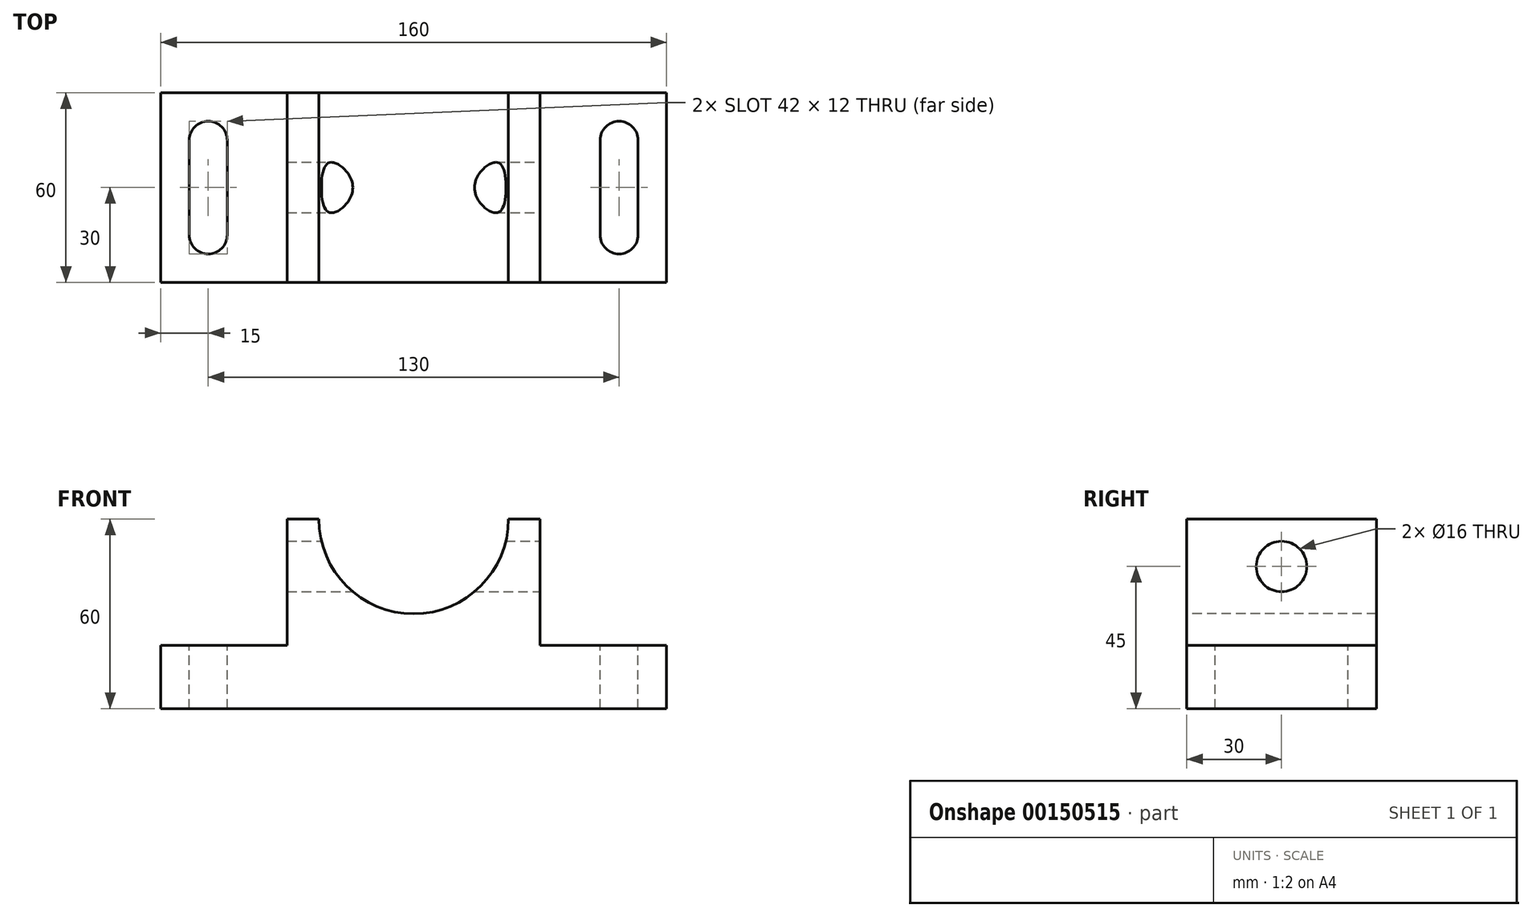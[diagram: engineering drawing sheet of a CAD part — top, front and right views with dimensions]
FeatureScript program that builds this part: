
annotation { "Feature Type Name" : "Feature", "Feature Type Description" : "" }
export const myFeature = defineFeature(function(context is Context, id is Id, definition is map)
    precondition{}
    {
        {
            var Q0;
            Q0=qCreatedBy(makeId("Top.planeOp"),FACE);
            var sketch = newSketch(context, id + "F0", { "sketchPlane" : qUnion([Q0])});
            skLineSegment(sketch, "E0.bottom", {"start": v(80, -30) * mm, "end": v(-80, -30) * mm});
            skLineSegment(sketch, "E0.top", {"start": v(80, 30) * mm, "end": v(-80, 30) * mm});
            skLineSegment(sketch, "E0.left", {"start": v(80, -30) * mm, "end": v(80, 30) * mm});
            skLineSegment(sketch, "E0.right", {"start": v(-80, -30) * mm, "end": v(-80, 30) * mm});
            skPoint(sketch, "E0.middle", {"position": v(0, 0) * mm});
            skSolve(sketch);
        }
        {
            var Q0;
            Q0 = qSketchRegion(id + "F0", true);
            extrude(context, id + "F1", {"entities" : qUnion([Q0]), "depth" : 20 * mm});
        }
        {
            var Q0;
            Q0=makeQuery(id+"F1.opExtrude","CAP_FACE",FACE,{"disambiguationData":[OSD([sQuery(id+"F0.wireOp",EDGE,"E0.bottom"),sQuery(id+"F0.wireOp",EDGE,"E0.top"),sQuery(id+"F0.wireOp",EDGE,"E0.left"),sQuery(id+"F0.wireOp",EDGE,"E0.right")])],"isStart":false});
            var sketch = newSketch(context, id + "F2", { "sketchPlane" : qUnion([Q0])});
            skLineSegment(sketch, "E1.left", {"start": v(-59, -15) * mm, "end": v(-59, 15) * mm});
            skLineSegment(sketch, "E1.right", {"start": v(-71, -15) * mm, "end": v(-71, 15) * mm});
            skPoint(sketch, "E1.middle", {"position": v(-65, 0) * mm});
            skLineSegment(sketch, "E2.left", {"start": v(71, -15) * mm, "end": v(71, 15) * mm});
            skLineSegment(sketch, "E2.right", {"start": v(59, -15) * mm, "end": v(59, 15) * mm});
            skPoint(sketch, "E2.middle", {"position": v(65, 0) * mm});
            skArc(sketch, "E3", {"start": v(-59, 15) * mm, "mid": v(-65, 21) * mm, "end": v(-71, 15) * mm});
            skArc(sketch, "E4", {"start": v(-71, -15) * mm, "mid": v(-65, -21) * mm, "end": v(-59, -15) * mm});
            skArc(sketch, "E5", {"start": v(71, 15) * mm, "mid": v(65, 21) * mm, "end": v(59, 15) * mm});
            skArc(sketch, "E6", {"start": v(59, -15) * mm, "mid": v(65, -21) * mm, "end": v(71, -15) * mm});
            skLineSegment(sketch, "E7.bottom", {"start": v(40, -30) * mm, "end": v(-40, -30) * mm});
            skLineSegment(sketch, "E7.top", {"start": v(40, 30) * mm, "end": v(-40, 30) * mm});
            skLineSegment(sketch, "E7.left", {"start": v(40, -30) * mm, "end": v(40, 30) * mm});
            skLineSegment(sketch, "E7.right", {"start": v(-40, -30) * mm, "end": v(-40, 30) * mm});
            skPoint(sketch, "E7.middle", {"position": v(0, 0) * mm});
            skSolve(sketch);
        }
        {
            var Q0;
            Q0=makeQuery(id+"F2.imprint","IMPRINT",FACE,{"disambiguationData":[TD([[makeQuery(id+"F2.imprint","IMPRINT",EDGE,{"derivedFrom":sQuery(id+"F2.wireOp",EDGE,"E1.left")}),1.0]])]});
            var Q1;
            Q1=makeQuery(id+"F2.imprint","IMPRINT",FACE,{"disambiguationData":[TD([[makeQuery(id+"F2.imprint","IMPRINT",EDGE,{"derivedFrom":sQuery(id+"F2.wireOp",EDGE,"E2.left")}),1.0]])]});
            extrude(context, id + "F3", {"entities" : qUnion([Q0, Q1]), "operationType" : NewBodyOperationType.REMOVE, "endBound" : BoundingType.THROUGH_ALL, "oppositeDirection" : true, "depth" : 25 * mm});
        }
        {
            var Q0;
            Q0=makeQuery(id+"F1.opExtrude","CAP_FACE",FACE,{"disambiguationData":[OSD([sQuery(id+"F0.wireOp",EDGE,"E0.bottom"),sQuery(id+"F0.wireOp",EDGE,"E0.top"),sQuery(id+"F0.wireOp",EDGE,"E0.left"),sQuery(id+"F0.wireOp",EDGE,"E0.right")])],"isStart":false});
            var sketch = newSketch(context, id + "F4", { "sketchPlane" : qUnion([Q0])});
            skLineSegment(sketch, "E8.bottom", {"start": v(145.81, -60) * mm, "end": v(65.81, -60) * mm});
            skLineSegment(sketch, "E8.top", {"start": v(145.81, -60) * mm, "end": v(65.81, -60) * mm});
            skLineSegment(sketch, "E8.left", {"start": v(65.81, -60) * mm, "end": v(145.81, -60) * mm});
            skLineSegment(sketch, "E8.right", {"start": v(65.81, -60) * mm, "end": v(145.81, -60) * mm});
            skPoint(sketch, "E8.middle", {"position": v(0, 0) * mm});
            skLineSegment(sketch, "E9.bottom", {"start": v(40, -30) * mm, "end": v(-40, -30) * mm});
            skLineSegment(sketch, "E9.top", {"start": v(40, 30) * mm, "end": v(-40, 30) * mm});
            skLineSegment(sketch, "E9.left", {"start": v(40, -30) * mm, "end": v(40, 30) * mm});
            skLineSegment(sketch, "E9.right", {"start": v(-40, -30) * mm, "end": v(-40, 30) * mm});
            skSolve(sketch);
        }
        {
            var Q0;
            Q0 = qSketchRegion(id + "F4", true);
            extrude(context, id + "F5", {"entities" : qUnion([Q0]), "operationType" : NewBodyOperationType.ADD, "depth" : 40 * mm});
        }
        {
            var Q0;
            Q0=makeQuery(id+"F5.opExtrude","SWEPT_FACE",FACE,{"disambiguationData":[OSD([sQuery(id+"F4.wireOp",EDGE,"E9.left")])]});
            var sketch = newSketch(context, id + "F6", { "sketchPlane" : qUnion([Q0])});
            skCircle(sketch, "E10", {"center": v(0, 45) * mm, "radius": 8 * mm});
            skSolve(sketch);
        }
        {
            var Q0;
            Q0=makeQuery(id+"F6.imprint","IMPRINT",FACE,{"disambiguationData":[TD([[makeQuery(id+"F6.imprint","IMPRINT",EDGE,{"derivedFrom":sQuery(id+"F6.wireOp",EDGE,"E10")}),1.0]])]});
            extrude(context, id + "F7", {"entities" : qUnion([Q0]), "operationType" : NewBodyOperationType.REMOVE, "endBound" : BoundingType.THROUGH_ALL, "oppositeDirection" : true, "depth" : 25 * mm});
        }
        {
            var Q0;
            Q0=makeQuery(id+"F5.boolean.opBoolean","MERGE",FACE,{"derivedFrom":[makeQuery(id+"F1.opExtrude","SWEPT_FACE",FACE,{"disambiguationData":[OSD([sQuery(id+"F0.wireOp",EDGE,"E0.bottom")])]}),makeQuery(id+"F5.opExtrude","SWEPT_FACE",FACE,{"disambiguationData":[OSD([sQuery(id+"F4.wireOp",EDGE,"E9.bottom")])]})]});
            var sketch = newSketch(context, id + "F8", { "sketchPlane" : qUnion([Q0])});
            skCircle(sketch, "E11", {"center": v(0, 60) * mm, "radius": 30 * mm});
            skLineSegment(sketch, "E12", {"start": v(-30, 60) * mm, "end": v(30, 60) * mm});
            skSolve(sketch);
        }
        {
            var Q0;
            Q0 = qSketchRegion(id + "F8", true);
            extrude(context, id + "F9", {"entities" : qUnion([Q0]), "operationType" : NewBodyOperationType.REMOVE, "endBound" : BoundingType.THROUGH_ALL, "oppositeDirection" : true, "depth" : 25 * mm});
        }
    });
